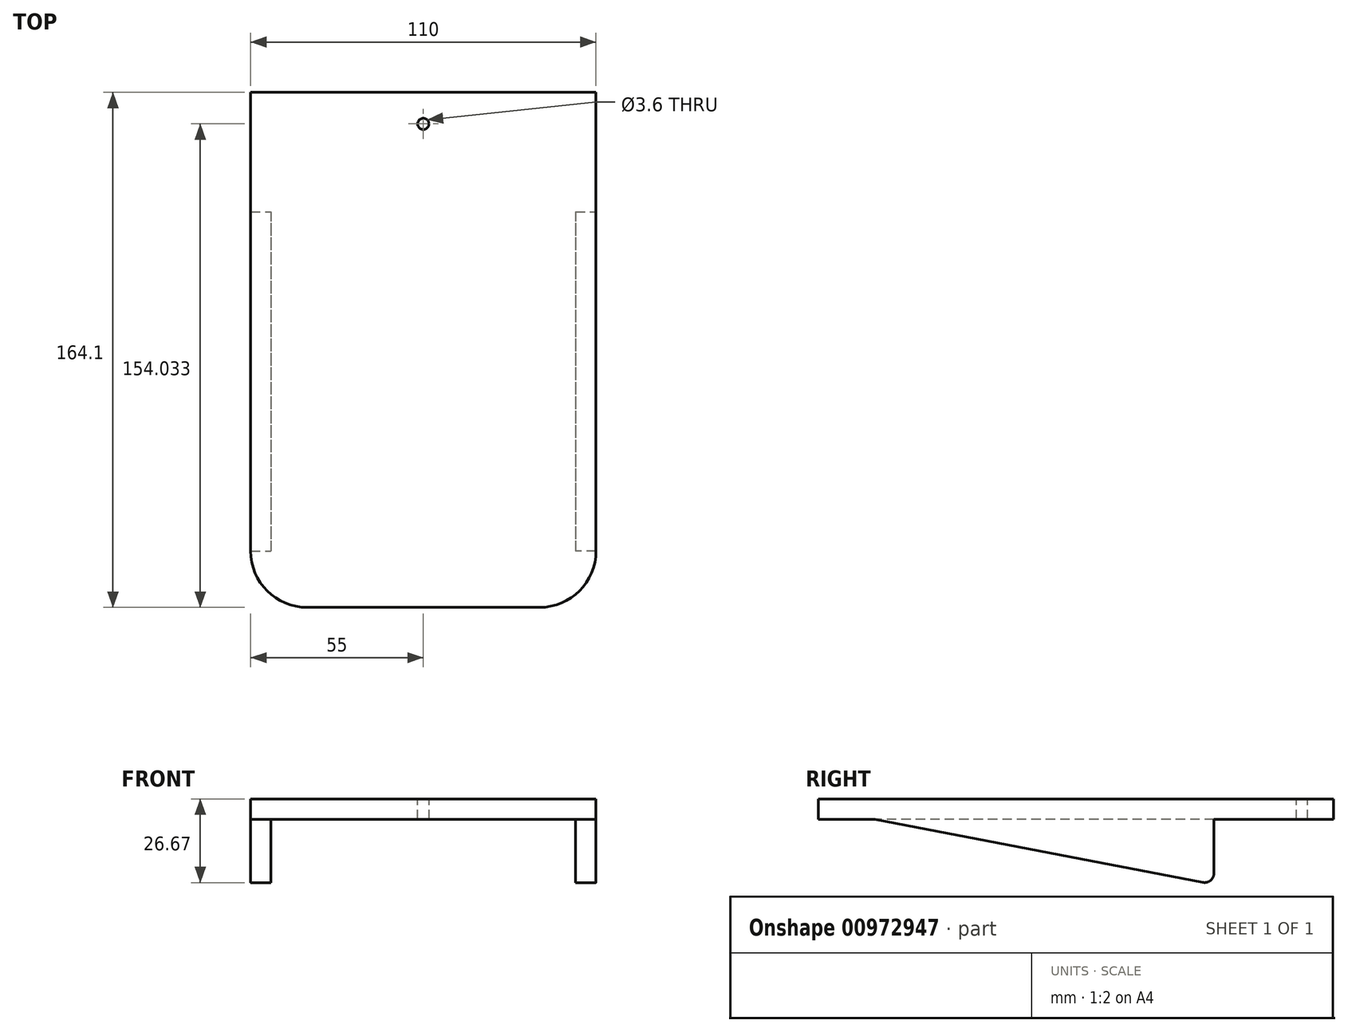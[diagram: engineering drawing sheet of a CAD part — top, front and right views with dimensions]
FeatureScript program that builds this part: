
annotation { "Feature Type Name" : "Feature", "Feature Type Description" : "" }
export const myFeature = defineFeature(function(context is Context, id is Id, definition is map)
    precondition{}
    {
        {
            var Q0;
            Q0=qCreatedBy(makeId("Top.planeOp"),FACE);
            var sketch = newSketch(context, id + "F0", { "sketchPlane" : qUnion([Q0])});
            skLineSegment(sketch, "E0.bottom", {"start": v(0, 0) * mm, "end": v(110, 0) * mm});
            skLineSegment(sketch, "E0.top", {"start": v(0, -126) * mm, "end": v(110, -126) * mm});
            skLineSegment(sketch, "E0.left", {"start": v(0, 0) * mm, "end": v(0, -126) * mm});
            skLineSegment(sketch, "E0.right", {"start": v(110, 0) * mm, "end": v(110, -126) * mm});
            skSolve(sketch);
        }
        {
            var Q0;
            Q0 = qSketchRegion(id + "F0", true);
            extrude(context, id + "F1", {"entities" : qUnion([Q0]), "depth" : 6.5 * mm, "offsetDistance" : 25 * mm});
        }
        {
            var Q0;
            Q0=makeQuery(id+"F1.opExtrude","SWEPT_FACE",FACE,{"disambiguationData":[OSD([sQuery(id+"F0.wireOp",EDGE,"E0.bottom")])]});
            var sketch = newSketch(context, id + "F2", { "sketchPlane" : qUnion([Q0])});
            skLineSegment(sketch, "E1.bottom", {"start": v(-110, 6.5) * mm, "end": v(0, 6.5) * mm});
            skLineSegment(sketch, "E1.top", {"start": v(-110, 0) * mm, "end": v(0, 0) * mm});
            skLineSegment(sketch, "E1.left", {"start": v(-110, 6.5) * mm, "end": v(-110, 0) * mm});
            skLineSegment(sketch, "E1.right", {"start": v(0, 6.5) * mm, "end": v(0, 0) * mm});
            skSolve(sketch);
        }
        {
            var Q0;
            Q0 = qSketchRegion(id + "F2", true);
            extrude(context, id + "F3", {"entities" : qUnion([Q0]), "operationType" : NewBodyOperationType.ADD, "depth" : 38.1 * mm, "offsetDistance" : 25 * mm});
        }
        {
            var Q0;
            Q0=makeQuery(id+"F3.boolean.opBoolean","MERGE",FACE,{"derivedFrom":[makeQuery(id+"F1.opExtrude","CAP_FACE",FACE,{"disambiguationData":[OSD([sQuery(id+"F0.wireOp",EDGE,"E0.bottom"),sQuery(id+"F0.wireOp",EDGE,"E0.top"),sQuery(id+"F0.wireOp",EDGE,"E0.left"),sQuery(id+"F0.wireOp",EDGE,"E0.right")])],"isStart":false}),makeQuery(id+"F3.opExtrude","SWEPT_FACE",FACE,{"disambiguationData":[OSD([sQuery(id+"F2.wireOp",EDGE,"E1.bottom")])]})]});
            var sketch = newSketch(context, id + "F4", { "sketchPlane" : qUnion([Q0])});
            skLineSegment(sketch, "E2", {"start": v(0, 38.1) * mm, "end": v(110, 38.1) * mm});
            skCircle(sketch, "E3", {"center": v(55, 28.03) * mm, "radius": 1.8 * mm});
            skPoint(sketch, "E3.centerSnap0", {"position": v(55, 38.1) * mm});
            skSolve(sketch);
        }
        {
            var Q0;
            Q0 = qSketchRegion(id + "F4", true);
            extrude(context, id + "F5", {"entities" : qUnion([Q0]), "operationType" : NewBodyOperationType.REMOVE, "oppositeDirection" : true, "depth" : 14.3 * mm, "offsetDistance" : 25 * mm});
        }
        {
            var Q0;
            Q0=makeQuery(id+"F1.opExtrude","SWEPT_EDGE",EDGE,{"disambiguationData":[OSD([sQuery(id+"F0.wireOp",EDGE,"E0.top"),sQuery(id+"F0.wireOp",EDGE,"E0.right")])]});
            fillet(context, id + "F6", {"entities" : qUnion([Q0]), "radius" : 18 * mm, "tangentPropagation" : true, "allowEdgeOverflow" : false});
        }
        {
            var Q0;
            Q0=makeQuery(id+"F1.opExtrude","SWEPT_EDGE",EDGE,{"disambiguationData":[OSD([sQuery(id+"F0.wireOp",EDGE,"E0.top"),sQuery(id+"F0.wireOp",EDGE,"E0.left")])]});
            fillet(context, id + "F7", {"entities" : qUnion([Q0]), "radius" : 18 * mm, "tangentPropagation" : true, "allowEdgeOverflow" : false});
        }
        {
            var Q0;
            Q0=makeQuery(id+"F3.boolean.opBoolean","MERGE",FACE,{"derivedFrom":[makeQuery(id+"F1.opExtrude","CAP_FACE",FACE,{"disambiguationData":[OSD([sQuery(id+"F0.wireOp",EDGE,"E0.bottom"),sQuery(id+"F0.wireOp",EDGE,"E0.top"),sQuery(id+"F0.wireOp",EDGE,"E0.left"),sQuery(id+"F0.wireOp",EDGE,"E0.right")])],"isStart":true}),makeQuery(id+"F3.opExtrude","SWEPT_FACE",FACE,{"disambiguationData":[OSD([sQuery(id+"F2.wireOp",EDGE,"E1.top")])]})]});
            var sketch = newSketch(context, id + "F8", { "sketchPlane" : qUnion([Q0])});
            skLineSegment(sketch, "E4.bottom", {"start": v(0, -38.1) * mm, "end": v(6.5, -38.1) * mm});
            skLineSegment(sketch, "E4.top", {"start": v(0, 108) * mm, "end": v(6.5, 108) * mm});
            skLineSegment(sketch, "E4.left", {"start": v(0, -38.1) * mm, "end": v(0, 108) * mm});
            skLineSegment(sketch, "E4.right", {"start": v(6.5, -38.1) * mm, "end": v(6.5, 108) * mm});
            skLineSegment(sketch, "E5.bottom", {"start": v(110, -38.1) * mm, "end": v(103.5, -38.1) * mm});
            skLineSegment(sketch, "E5.top", {"start": v(110, 108) * mm, "end": v(103.5, 108) * mm});
            skLineSegment(sketch, "E5.left", {"start": v(110, -38.1) * mm, "end": v(110, 108) * mm});
            skLineSegment(sketch, "E5.right", {"start": v(103.5, -38.1) * mm, "end": v(103.5, 108) * mm});
            skSolve(sketch);
        }
        {
            var Q0;
            Q0 = qSketchRegion(id + "F8", true);
            extrude(context, id + "F9", {"entities" : qUnion([Q0]), "operationType" : NewBodyOperationType.ADD, "depth" : 20.8 * mm, "offsetDistance" : 25 * mm});
        }
        {
            var Q0;
            Q0=makeQuery(id+"F9.boolean.opBoolean","MERGE",FACE,{"derivedFrom":[makeQuery(id+"F3.boolean.opBoolean","MERGE",FACE,{"derivedFrom":[makeQuery(id+"F1.opExtrude","SWEPT_FACE",FACE,{"disambiguationData":[OSD([sQuery(id+"F0.wireOp",EDGE,"E0.right")])]}),makeQuery(id+"F3.opExtrude","SWEPT_FACE",FACE,{"disambiguationData":[OSD([sQuery(id+"F2.wireOp",EDGE,"E1.left")])]})]}),makeQuery(id+"F9.opExtrude","SWEPT_FACE",FACE,{"disambiguationData":[OSD([sQuery(id+"F8.wireOp",EDGE,"E5.left")])]})]});
            var sketch = newSketch(context, id + "F10", { "sketchPlane" : qUnion([Q0])});
            skLineSegment(sketch, "E6", {"start": v(-108, 0) * mm, "end": v(0, -20.8) * mm});
            skLineSegment(sketch, "E7", {"start": v(0, -20.8) * mm, "end": v(-108, -20.8) * mm});
            skLineSegment(sketch, "E8", {"start": v(-108, -20.8) * mm, "end": v(-108, 0) * mm});
            skLineSegment(sketch, "E9", {"start": v(0, -20.8) * mm, "end": v(0, 0) * mm});
            skLineSegment(sketch, "E10", {"start": v(0, 0) * mm, "end": v(38.1, 0) * mm});
            skLineSegment(sketch, "E11", {"start": v(38.1, 0) * mm, "end": v(38.1, -20.8) * mm});
            skLineSegment(sketch, "E12", {"start": v(38.1, -20.8) * mm, "end": v(0, -20.8) * mm});
            skSolve(sketch);
        }
        {
            var Q0;
            Q0 = qSketchRegion(id + "F10", true);
            extrude(context, id + "F11", {"entities" : qUnion([Q0]), "operationType" : NewBodyOperationType.REMOVE, "oppositeDirection" : true, "depth" : 133.7 * mm, "offsetDistance" : 25 * mm});
        }
        {
            var Q0;
            {var subQ0=sQuery(id+"F10.wireOp",EDGE,"E12");var subQ1=sQuery(id+"F10.wireOp",EDGE,"E9");var subQ2=sQuery(id+"F10.wireOp",EDGE,"E7");var subQ3=sQuery(id+"F10.wireOp",EDGE,"E6");Q0=makeQuery(id+"F11.boolean.opBoolean","MERGE",EDGE,{"disambiguationData":[OD(0.0)],"derivedFrom":[],"fromTools":[makeQuery(id+"F11.opExtrude","SWEPT_EDGE",EDGE,{"disambiguationData":[OSD([subQ3,subQ2,subQ1,subQ0]),OD(0.0)]}),makeQuery(id+"F11.opExtrude","SWEPT_EDGE",EDGE,{"disambiguationData":[OSD([subQ3,subQ2,subQ1,subQ0]),OD(1.0)]})]});}
            fillet(context, id + "F12", {"entities" : qUnion([Q0]), "radius" : 3 * mm, "tangentPropagation" : true, "allowEdgeOverflow" : false});
        }
        {
            var Q0;
            {var subQ0=sQuery(id+"F10.wireOp",EDGE,"E12");var subQ1=sQuery(id+"F10.wireOp",EDGE,"E9");var subQ2=sQuery(id+"F10.wireOp",EDGE,"E7");var subQ3=sQuery(id+"F10.wireOp",EDGE,"E6");Q0=makeQuery(id+"F11.boolean.opBoolean","MERGE",EDGE,{"disambiguationData":[OD(1.0)],"derivedFrom":[],"fromTools":[makeQuery(id+"F11.opExtrude","SWEPT_EDGE",EDGE,{"disambiguationData":[OSD([subQ3,subQ2,subQ1,subQ0]),OD(0.0)]}),makeQuery(id+"F11.opExtrude","SWEPT_EDGE",EDGE,{"disambiguationData":[OSD([subQ3,subQ2,subQ1,subQ0]),OD(1.0)]})]});}
            fillet(context, id + "F13", {"entities" : qUnion([Q0]), "radius" : 3 * mm, "tangentPropagation" : true, "allowEdgeOverflow" : false});
        }
    });
